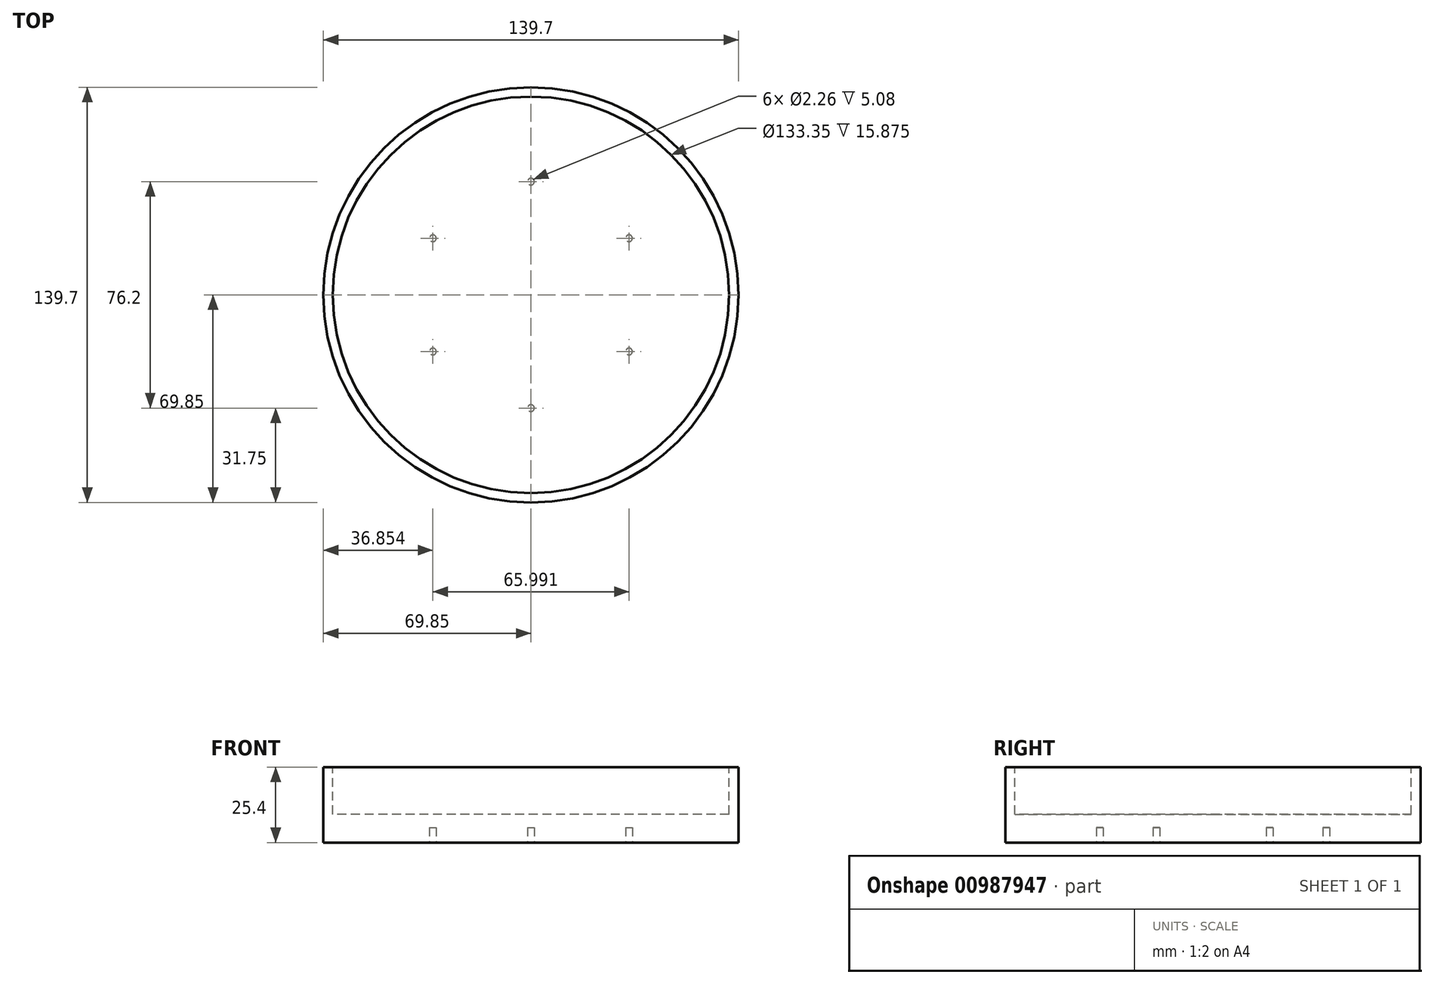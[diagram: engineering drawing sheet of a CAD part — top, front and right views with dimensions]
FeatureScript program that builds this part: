
annotation { "Feature Type Name" : "Feature", "Feature Type Description" : "" }
export const myFeature = defineFeature(function(context is Context, id is Id, definition is map)
    precondition{}
    {
        {
            var Q0;
            Q0=qCreatedBy(makeId("Top.planeOp"),FACE);
            var sketch = newSketch(context, id + "F0", { "sketchPlane" : qUnion([Q0])});
            skCircle(sketch, "E0", {"center": v(0, 0) * mm, "radius": 69.85 * mm});
            skSolve(sketch);
        }
        {
            var Q0;
            Q0 = qSketchRegion(id + "F0", true);
            extrude(context, id + "F1", {"entities" : qUnion([Q0]), "depth" : 25.4 * mm, "offsetDistance" : 25.4 * mm});
        }
        {
            var Q0;
            Q0=makeQuery(id+"F1.opExtrude","CAP_FACE",FACE,{"disambiguationData":[OSD([sQuery(id+"F0.wireOp",EDGE,"E0")])],"isStart":false});
            var sketch = newSketch(context, id + "F2", { "sketchPlane" : qUnion([Q0])});
            skCircle(sketch, "E1", {"center": v(0, 0) * mm, "radius": 66.68 * mm});
            skSolve(sketch);
        }
        {
            var Q0;
            Q0 = qSketchRegion(id + "F2", true);
            extrude(context, id + "F3", {"entities" : qUnion([Q0]), "operationType" : NewBodyOperationType.REMOVE, "oppositeDirection" : true, "depth" : 15.88 * mm, "offsetDistance" : 25.4 * mm});
        }
        {
            var Q0;
            Q0=makeQuery(id+"F1.opExtrude","CAP_FACE",FACE,{"disambiguationData":[OSD([sQuery(id+"F0.wireOp",EDGE,"E0")])],"isStart":true});
            var sketch = newSketch(context, id + "F4", { "sketchPlane" : qUnion([Q0])});
            skCircle(sketch, "E2", {"center": v(0, 38.1) * mm, "radius": 1.13 * mm});
            skCircle(sketch, "E3.1.0", {"center": v(-33, 19.05) * mm, "radius": 1.13 * mm});
            skCircle(sketch, "E3.2.0", {"center": v(-33, -19.05) * mm, "radius": 1.13 * mm});
            skCircle(sketch, "E3.3.0", {"center": v(0, -38.1) * mm, "radius": 1.13 * mm});
            skCircle(sketch, "E3.4.0", {"center": v(33, -19.05) * mm, "radius": 1.13 * mm});
            skCircle(sketch, "E3.5.0", {"center": v(33, 19.05) * mm, "radius": 1.13 * mm});
            skPoint(sketch, "E3.center", {"position": v(0, 0) * mm});
            skSolve(sketch);
        }
        {
            var Q0;
            Q0 = qSketchRegion(id + "F4", true);
            extrude(context, id + "F5", {"entities" : qUnion([Q0]), "operationType" : NewBodyOperationType.REMOVE, "oppositeDirection" : true, "depth" : 5.08 * mm, "offsetDistance" : 25.4 * mm});
        }
    });
